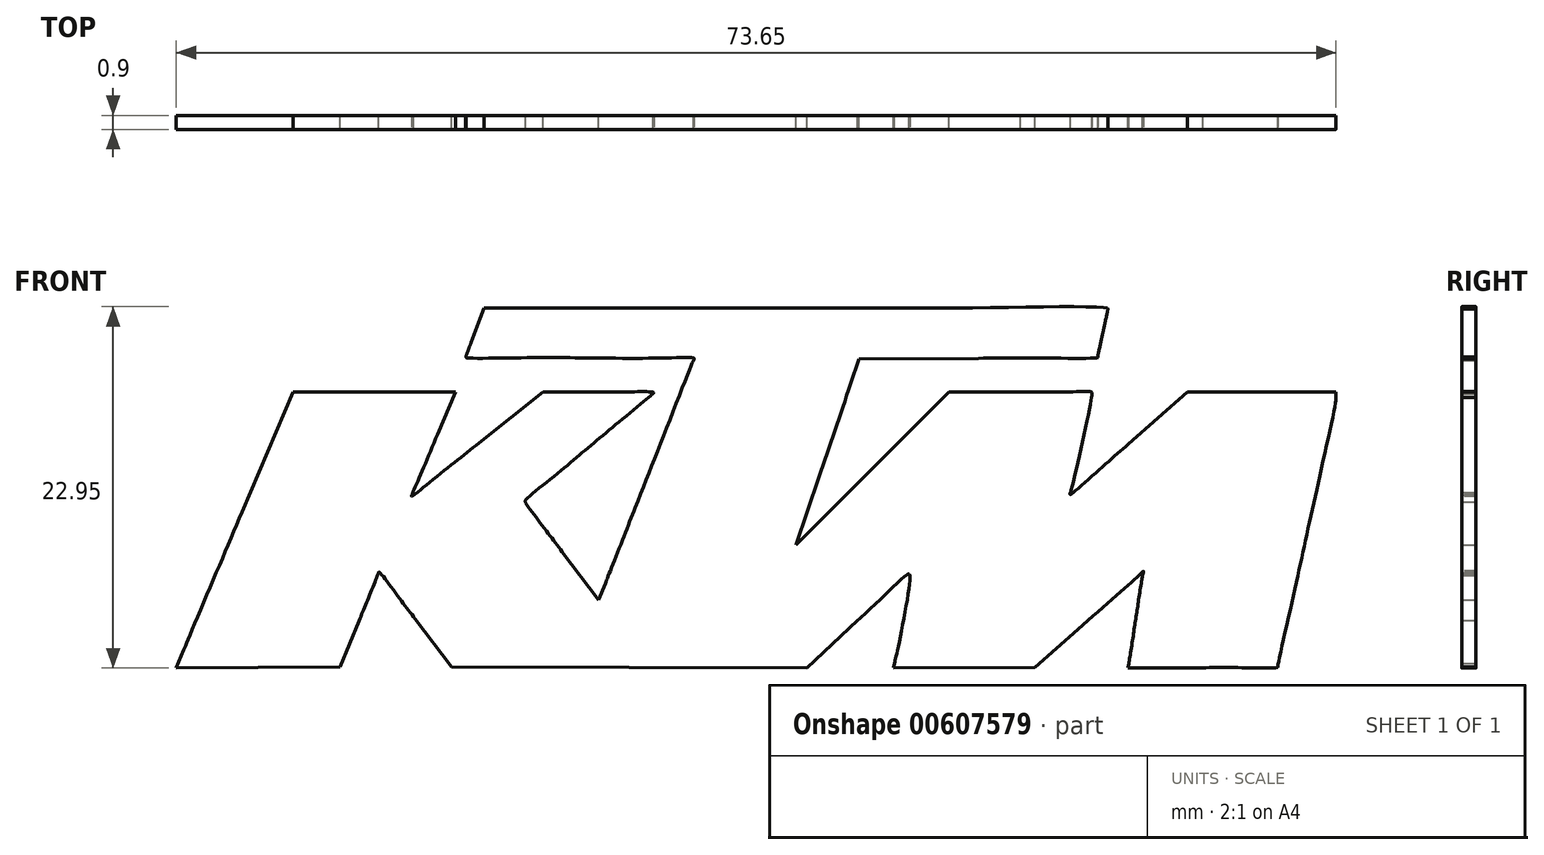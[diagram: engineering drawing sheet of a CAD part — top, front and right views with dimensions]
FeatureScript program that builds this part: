
annotation { "Feature Type Name" : "Feature", "Feature Type Description" : "" }
export const myFeature = defineFeature(function(context is Context, id is Id, definition is map)
    precondition{}
    {
        {
            var Q0;
            Q0=qCreatedBy(makeId("Front.planeOp"),FACE);
            var sketch = newSketch(context, id + "F0", { "sketchPlane" : qUnion([Q0])});
            skFitSpline(sketch, "E0", {"points": [v(-80.79, -22.92) * mm, v(-80.21, -21.55) * mm, v(-76.5, -12.79) * mm, v(-72.55, -3.44) * mm]});
            skFitSpline(sketch, "E1", {"points": [v(-44.95, 7.55) * mm, v(-48.16, -0.05) * mm, v(-48.62, -1.2) * mm, v(-48.34, -1.03) * mm]});
            skFitSpline(sketch, "E2", {"points": [v(-48.34, -1.03) * mm, v(-48.22, -0.95) * mm, v(-44.06, 2.36) * mm, v(-39.1, 6.33) * mm]});
            skLineSegment(sketch, "E3", {"start": v(-72.55, -3.44) * mm, "end": v(-65.35, 13.54) * mm});
            skLineSegment(sketch, "E4", {"start": v(-65.35, 13.54) * mm, "end": v(-53.88, 13.55) * mm});
            skLineSegment(sketch, "E5", {"start": v(-53.88, 13.55) * mm, "end": v(-42.42, 13.55) * mm});
            skLineSegment(sketch, "E6", {"start": v(-42.42, 13.55) * mm, "end": v(-44.95, 7.55) * mm});
            skFitSpline(sketch, "E7", {"points": [v(-22.19, 13.55) * mm, v(-17.45, 13.55) * mm, v(-14.4, 13.45) * mm, v(-14.57, 13.3) * mm]});
            skFitSpline(sketch, "E8", {"points": [v(-14.57, 13.3) * mm, v(-14.71, 13.15) * mm, v(-18.83, 9.7) * mm, v(-23.72, 5.63) * mm]});
            skFitSpline(sketch, "E9", {"points": [v(-23.72, 5.63) * mm, v(-28.61, 1.56) * mm, v(-32.58, -1.89) * mm, v(-32.54, -2.03) * mm]});
            skFitSpline(sketch, "E10", {"points": [v(-32.54, -2.03) * mm, v(-32.5, -2.17) * mm, v(-30.16, -5.33) * mm, v(-27.34, -9.05) * mm]});
            skLineSegment(sketch, "E11", {"start": v(-39.1, 6.33) * mm, "end": v(-30.07, 13.55) * mm});
            skLineSegment(sketch, "E12", {"start": v(-30.07, 13.55) * mm, "end": v(-22.19, 13.55) * mm});
            skFitSpline(sketch, "E13", {"points": [v(-21.26, -13.48) * mm, v(-20.74, -12.2) * mm, v(-18.84, -7.4) * mm, v(-17.04, -2.82) * mm]});
            skFitSpline(sketch, "E14", {"points": [v(-17.04, -2.82) * mm, v(-12.65, 8.37) * mm, v(-9.03, 17.56) * mm, v(-8.85, 18) * mm]});
            skFitSpline(sketch, "E15", {"points": [v(-8.85, 18) * mm, v(-8.74, 18.27) * mm, v(-12.04, 18.35) * mm, v(-24.82, 18.35) * mm]});
            skFitSpline(sketch, "E16", {"points": [v(-24.82, 18.35) * mm, v(-33.69, 18.35) * mm, v(-40.94, 18.4) * mm, v(-40.94, 18.46) * mm]});
            skFitSpline(sketch, "E17", {"points": [v(-40.94, 18.46) * mm, v(-40.94, 18.51) * mm, v(-40.6, 19.43) * mm, v(-40.2, 20.5) * mm]});
            skFitSpline(sketch, "E18", {"points": [v(-40.2, 20.5) * mm, v(-39.8, 21.57) * mm, v(-39.22, 23.1) * mm, v(-38.92, 23.92) * mm]});
            skLineSegment(sketch, "E19", {"start": v(-27.34, -9.05) * mm, "end": v(-22.2, -15.82) * mm});
            skLineSegment(sketch, "E20", {"start": v(-22.2, -15.82) * mm, "end": v(-21.26, -13.48) * mm});
            skFitSpline(sketch, "E21", {"points": [v(5.65, 25.4) * mm, v(29.85, 25.4) * mm, v(49.65, 25.34) * mm, v(49.65, 25.26) * mm]});
            skFitSpline(sketch, "E22", {"points": [v(49.65, 25.26) * mm, v(49.65, 25.18) * mm, v(49.34, 23.64) * mm, v(48.95, 21.85) * mm]});
            skFitSpline(sketch, "E23", {"points": [v(48.95, 21.85) * mm, v(48.56, 20.05) * mm, v(48.24, 18.53) * mm, v(48.24, 18.47) * mm]});
            skFitSpline(sketch, "E24", {"points": [v(48.24, 18.47) * mm, v(48.24, 18.4) * mm, v(40.67, 18.32) * mm, v(31.4, 18.28) * mm]});
            skLineSegment(sketch, "E25", {"start": v(-38.92, 23.92) * mm, "end": v(-38.36, 25.4) * mm});
            skLineSegment(sketch, "E26", {"start": v(-38.36, 25.4) * mm, "end": v(5.65, 25.4) * mm});
            skFitSpline(sketch, "E27", {"points": [v(13.37, 14.68) * mm, v(12.72, 12.74) * mm, v(10.7, 6.83) * mm, v(8.9, 1.56) * mm]});
            skLineSegment(sketch, "E28", {"start": v(31.4, 18.28) * mm, "end": v(14.57, 18.2) * mm});
            skLineSegment(sketch, "E29", {"start": v(14.57, 18.2) * mm, "end": v(13.37, 14.68) * mm});
            skFitSpline(sketch, "E30", {"points": [v(37.3, 13.55) * mm, v(44.63, 13.55) * mm, v(47.4, 13.46) * mm, v(47.4, 13.23) * mm]});
            skFitSpline(sketch, "E31", {"points": [v(47.4, 13.23) * mm, v(47.4, 12.9) * mm, v(44.66, 0.29) * mm, v(44.39, -0.66) * mm]});
            skFitSpline(sketch, "E32", {"points": [v(44.39, -0.66) * mm, v(44.3, -0.94) * mm, v(48, 2.13) * mm, v(52.58, 6.19) * mm]});
            skLineSegment(sketch, "E33", {"start": v(8.9, 1.56) * mm, "end": v(5.62, -8.04) * mm});
            skLineSegment(sketch, "E34", {"start": v(5.62, -8.04) * mm, "end": v(16.42, 2.75) * mm});
            skLineSegment(sketch, "E35", {"start": v(16.42, 2.75) * mm, "end": v(27.22, 13.55) * mm});
            skLineSegment(sketch, "E36", {"start": v(27.22, 13.55) * mm, "end": v(37.3, 13.55) * mm});
            skFitSpline(sketch, "E37", {"points": [v(81.83, 12.72) * mm, v(81.83, 12.26) * mm, v(79.99, 3.54) * mm, v(77.74, -6.65) * mm]});
            skFitSpline(sketch, "E38", {"points": [v(77.74, -6.65) * mm, v(75.48, -16.85) * mm, v(73.64, -25.24) * mm, v(73.64, -25.3) * mm]});
            skFitSpline(sketch, "E39", {"points": [v(73.64, -25.3) * mm, v(73.64, -25.35) * mm, v(68.88, -25.4) * mm, v(63.05, -25.4) * mm]});
            skLineSegment(sketch, "E40", {"start": v(52.58, 6.19) * mm, "end": v(60.92, 13.55) * mm});
            skLineSegment(sketch, "E41", {"start": v(60.92, 13.55) * mm, "end": v(71.37, 13.55) * mm});
            skLineSegment(sketch, "E42", {"start": v(71.37, 13.55) * mm, "end": v(81.83, 13.55) * mm});
            skLineSegment(sketch, "E43", {"start": v(81.83, 13.55) * mm, "end": v(81.83, 12.72) * mm});
            skFitSpline(sketch, "E44", {"points": [v(52.6, -24.76) * mm, v(52.69, -24.41) * mm, v(53.14, -21.59) * mm, v(53.6, -18.48) * mm]});
            skFitSpline(sketch, "E45", {"points": [v(53.6, -18.48) * mm, v(54.08, -15.38) * mm, v(54.51, -12.61) * mm, v(54.57, -12.34) * mm]});
            skFitSpline(sketch, "E46", {"points": [v(54.57, -12.34) * mm, v(54.7, -11.78) * mm, v(54.41, -12.02) * mm, v(45.42, -20) * mm]});
            skLineSegment(sketch, "E47", {"start": v(63.05, -25.4) * mm, "end": v(52.47, -25.4) * mm});
            skLineSegment(sketch, "E48", {"start": v(52.47, -25.4) * mm, "end": v(52.6, -24.76) * mm});
            skFitSpline(sketch, "E49", {"points": [v(19.54, -24.76) * mm, v(20.06, -22.54) * mm, v(21.75, -12.35) * mm, v(21.62, -12.23) * mm]});
            skFitSpline(sketch, "E50", {"points": [v(21.62, -12.23) * mm, v(21.54, -12.15) * mm, v(18.26, -15.08) * mm, v(14.33, -18.74) * mm]});
            skLineSegment(sketch, "E51", {"start": v(45.42, -20) * mm, "end": v(39.35, -25.38) * mm});
            skLineSegment(sketch, "E52", {"start": v(39.35, -25.38) * mm, "end": v(29.37, -25.39) * mm});
            skLineSegment(sketch, "E53", {"start": v(29.37, -25.39) * mm, "end": v(19.4, -25.4) * mm});
            skLineSegment(sketch, "E54", {"start": v(19.4, -25.4) * mm, "end": v(19.54, -24.76) * mm});
            skFitSpline(sketch, "E55", {"points": [v(-48.1, -18.51) * mm, v(-50.9, -14.8) * mm, v(-53.23, -11.89) * mm, v(-53.28, -12.02) * mm]});
            skFitSpline(sketch, "E56", {"points": [v(-53.28, -12.02) * mm, v(-53.33, -12.16) * mm, v(-54.56, -15.2) * mm, v(-56.02, -18.76) * mm]});
            skLineSegment(sketch, "E57", {"start": v(14.33, -18.74) * mm, "end": v(7.2, -25.4) * mm});
            skLineSegment(sketch, "E58", {"start": v(7.2, -25.4) * mm, "end": v(-17.9, -25.33) * mm});
            skLineSegment(sketch, "E59", {"start": v(-17.9, -25.33) * mm, "end": v(-43, -25.26) * mm});
            skLineSegment(sketch, "E60", {"start": v(-43, -25.26) * mm, "end": v(-48.1, -18.51) * mm});
            skLineSegment(sketch, "E61", {"start": v(-56.02, -18.76) * mm, "end": v(-58.67, -25.26) * mm});
            skLineSegment(sketch, "E62", {"start": v(-58.67, -25.26) * mm, "end": v(-70.25, -25.33) * mm});
            skLineSegment(sketch, "E63", {"start": v(-70.25, -25.33) * mm, "end": v(-81.83, -25.4) * mm});
            skLineSegment(sketch, "E64", {"start": v(-81.83, -25.4) * mm, "end": v(-80.79, -22.92) * mm});
            skSolve(sketch);
        }
        {
            var Q0;
            Q0=makeQuery(id+"F0.imprint","IMPRINT",FACE,{"disambiguationData":[TD([[makeQuery(id+"F0.imprint","IMPRINT",EDGE,{"derivedFrom":sQuery(id+"F0.wireOp",EDGE,"E0")}),-1.0]])]});
            extrude(context, id + "F1", {"entities" : qUnion([Q0]), "depth" : 2 * mm, "offsetDistance" : 25 * mm});
        }
        {
            var Q0;
            Q0=makeQuery(id+"F1.opExtrude","SWEPT_BODY",BODY,{"disambiguationData":[OSD([sQuery(id+"F0.wireOp",EDGE,"E0"),sQuery(id+"F0.wireOp",EDGE,"E1"),sQuery(id+"F0.wireOp",EDGE,"E2"),sQuery(id+"F0.wireOp",EDGE,"E3"),sQuery(id+"F0.wireOp",EDGE,"E4"),sQuery(id+"F0.wireOp",EDGE,"E5"),sQuery(id+"F0.wireOp",EDGE,"E6"),sQuery(id+"F0.wireOp",EDGE,"E7"),sQuery(id+"F0.wireOp",EDGE,"E8"),sQuery(id+"F0.wireOp",EDGE,"E9"),sQuery(id+"F0.wireOp",EDGE,"E10"),sQuery(id+"F0.wireOp",EDGE,"E11"),sQuery(id+"F0.wireOp",EDGE,"E12"),sQuery(id+"F0.wireOp",EDGE,"E13"),sQuery(id+"F0.wireOp",EDGE,"E14"),sQuery(id+"F0.wireOp",EDGE,"E15"),sQuery(id+"F0.wireOp",EDGE,"E16"),sQuery(id+"F0.wireOp",EDGE,"E17"),sQuery(id+"F0.wireOp",EDGE,"E18"),sQuery(id+"F0.wireOp",EDGE,"E19"),sQuery(id+"F0.wireOp",EDGE,"E20"),sQuery(id+"F0.wireOp",EDGE,"E21"),sQuery(id+"F0.wireOp",EDGE,"E22"),sQuery(id+"F0.wireOp",EDGE,"E23"),sQuery(id+"F0.wireOp",EDGE,"E24"),sQuery(id+"F0.wireOp",EDGE,"E25"),sQuery(id+"F0.wireOp",EDGE,"E26"),sQuery(id+"F0.wireOp",EDGE,"E27"),sQuery(id+"F0.wireOp",EDGE,"E28"),sQuery(id+"F0.wireOp",EDGE,"E29"),sQuery(id+"F0.wireOp",EDGE,"E30"),sQuery(id+"F0.wireOp",EDGE,"E31"),sQuery(id+"F0.wireOp",EDGE,"E32"),sQuery(id+"F0.wireOp",EDGE,"E33"),sQuery(id+"F0.wireOp",EDGE,"E34"),sQuery(id+"F0.wireOp",EDGE,"E35"),sQuery(id+"F0.wireOp",EDGE,"E36"),sQuery(id+"F0.wireOp",EDGE,"E37"),sQuery(id+"F0.wireOp",EDGE,"E38"),sQuery(id+"F0.wireOp",EDGE,"E39"),sQuery(id+"F0.wireOp",EDGE,"E40"),sQuery(id+"F0.wireOp",EDGE,"E41"),sQuery(id+"F0.wireOp",EDGE,"E42"),sQuery(id+"F0.wireOp",EDGE,"E43"),sQuery(id+"F0.wireOp",EDGE,"E44"),sQuery(id+"F0.wireOp",EDGE,"E45"),sQuery(id+"F0.wireOp",EDGE,"E46"),sQuery(id+"F0.wireOp",EDGE,"E47"),sQuery(id+"F0.wireOp",EDGE,"E48"),sQuery(id+"F0.wireOp",EDGE,"E49"),sQuery(id+"F0.wireOp",EDGE,"E50"),sQuery(id+"F0.wireOp",EDGE,"E51"),sQuery(id+"F0.wireOp",EDGE,"E52"),sQuery(id+"F0.wireOp",EDGE,"E53"),sQuery(id+"F0.wireOp",EDGE,"E54"),sQuery(id+"F0.wireOp",EDGE,"E55"),sQuery(id+"F0.wireOp",EDGE,"E56"),sQuery(id+"F0.wireOp",EDGE,"E57"),sQuery(id+"F0.wireOp",EDGE,"E58"),sQuery(id+"F0.wireOp",EDGE,"E59"),sQuery(id+"F0.wireOp",EDGE,"E60"),sQuery(id+"F0.wireOp",EDGE,"E61"),sQuery(id+"F0.wireOp",EDGE,"E62"),sQuery(id+"F0.wireOp",EDGE,"E63"),sQuery(id+"F0.wireOp",EDGE,"E64")])]});
            var Q1;
            Q1=qCreatedBy(makeId("Origin.pointOp"),VERTEX);
            transform(context, id + "F2", {"entities" : qUnion([Q0]), "transformType" : TransformType.SCALE_UNIFORMLY, "scale" : .45, "scalePoint" : qUnion([Q1]), "makeCopy" : false});
        }
    });
